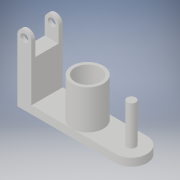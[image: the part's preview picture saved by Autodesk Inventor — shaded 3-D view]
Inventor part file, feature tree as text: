
AUTODESK INVENTOR PART (.ipt)
format: ipt  version: 2019 (Build 230136000, 136)  size: 161,280 bytes
history: native  units: in
note: dims shown in document units (in); Inventor stores cm internally (conversion verified against a paired STEP export)
features: extrude x5, sketch x5
ambient origin geometry x8: Origin, YZ Plane, XZ Plane, XY Plane, X Axis, Y Axis, Z Axis, Center Point
bodies: Solid1 (feature_tree)
feature tree (10):
  extrude  "Extrusion1"  Depth=0.1969in
  sketch  "Sketch2"  dims[d6=0.1772in d7=0.1969in]
  extrude  "Extrusion5"  Depth=0.1969in
  extrude  "Extrusion6"  Depth=0.3543in
  extrude  "Extrusion7"  Depth=0.7874in
  extrude  "Extrusion10"  Depth=0.7874in
  sketch  "Sketch1"  dims[d0=1.5748in d2=0.1969in]
  sketch  "Sketch7"  dims[d8=0.3543in d9=2.126in]
  sketch  "Sketch9"  dims[d10=0.7874in d11=0.0in d12=0.1181in]
  sketch  "Sketch12"  dims[d13=0.2559in d14=0.7874in d16=1.0236in d19=0.3937in d20=0.2205in d21=0.3937in d22=0.5984in d40=0.5512in d41=0.5512in d42=0.5906in d43=0.5512in d44=0.0in d47=1.2795in d48=0.9843in d49=0.0in d50=0.6299in d51=1.2205in d52=0.0in d65=0.1969in d66=0.0in d67=0.0in]
